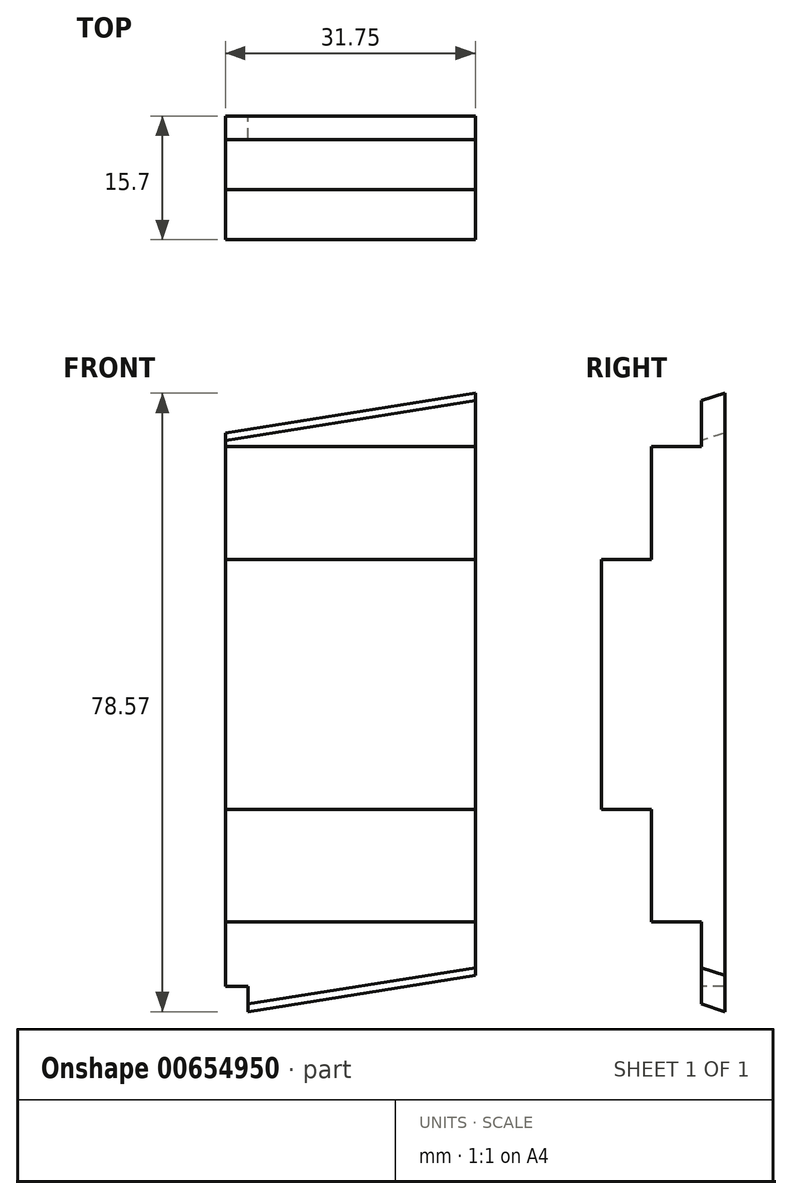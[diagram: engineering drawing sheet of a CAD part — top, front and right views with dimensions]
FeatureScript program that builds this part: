
annotation { "Feature Type Name" : "Feature", "Feature Type Description" : "" }
export const myFeature = defineFeature(function(context is Context, id is Id, definition is map)
    precondition{}
    {
        {
            var Q0;
            Q0=qCreatedBy(makeId("Front.planeOp"),FACE);
            var sketch = newSketch(context, id + "F0", { "sketchPlane" : qUnion([Q0])});
            skLineSegment(sketch, "E0.bottom", {"start": v(0, 0) * mm, "end": v(31.75, 0) * mm});
            skLineSegment(sketch, "E0.top", {"start": v(0, 67.31) * mm, "end": v(31.75, 67.31) * mm});
            skLineSegment(sketch, "E0.left", {"start": v(0, 0) * mm, "end": v(0, 67.31) * mm});
            skLineSegment(sketch, "E0.right", {"start": v(31.75, 0) * mm, "end": v(31.75, 67.31) * mm});
            skLineSegment(sketch, "E1", {"start": v(31.75, 67.31) * mm, "end": v(31.75, 72.4) * mm});
            skLineSegment(sketch, "E2", {"start": v(0, 67.31) * mm, "end": v(31.75, 72.4) * mm});
            skLineSegment(sketch, "E3", {"start": v(31.75, 0) * mm, "end": v(0, -5.08) * mm});
            skLineSegment(sketch, "E4", {"start": v(0, -5.08) * mm, "end": v(0, 0) * mm});
            skSolve(sketch);
        }
        {
            var Q0;
            Q0=makeQuery(id+"F0.imprint","IMPRINT",FACE,{"disambiguationData":[TD([[makeQuery(id+"F0.imprint","IMPRINT",EDGE,{"derivedFrom":sQuery(id+"F0.wireOp",EDGE,"E0.bottom")}),1.0]])]});
            var Q1;
            Q1=makeQuery(id+"F0.imprint","IMPRINT",FACE,{"disambiguationData":[TD([[makeQuery(id+"F0.imprint","IMPRINT",EDGE,{"derivedFrom":sQuery(id+"F0.wireOp",EDGE,"E0.top")}),1.0]])]});
            var Q2;
            Q2=makeQuery(id+"F0.imprint","IMPRINT",FACE,{"disambiguationData":[TD([[makeQuery(id+"F0.imprint","IMPRINT",EDGE,{"derivedFrom":sQuery(id+"F0.wireOp",EDGE,"E0.bottom")}),-1.0]])]});
            extrude(context, id + "F1", {"entities" : qUnion([Q0, Q1, Q2]), "depth" : 3.17 * mm, "offsetDistance" : 25.4 * mm});
        }
        {
            var Q0;
            Q0=makeQuery(id+"F1.opExtrude","CAP_FACE",FACE,{"disambiguationData":[OSD([sQuery(id+"F0.wireOp",EDGE,"E0.left"),sQuery(id+"F0.wireOp",EDGE,"E0.right"),sQuery(id+"F0.wireOp",EDGE,"E1"),sQuery(id+"F0.wireOp",EDGE,"E2"),sQuery(id+"F0.wireOp",EDGE,"E3"),sQuery(id+"F0.wireOp",EDGE,"E4")])],"isStart":false});
            var sketch = newSketch(context, id + "F2", { "sketchPlane" : qUnion([Q0])});
            skLineSegment(sketch, "E5.bottom", {"start": v(0, -5.08) * mm, "end": v(2.54, -5.08) * mm});
            skLineSegment(sketch, "E5.top", {"start": v(0, -2.54) * mm, "end": v(2.54, -2.54) * mm});
            skLineSegment(sketch, "E5.left", {"start": v(0, -5.08) * mm, "end": v(0, -2.54) * mm});
            skLineSegment(sketch, "E5.right", {"start": v(2.54, -5.08) * mm, "end": v(2.54, -2.54) * mm});
            skLineSegment(sketch, "E6", {"start": v(0, -2.36) * mm, "end": v(2.72, -2.36) * mm});
            skLineSegment(sketch, "E7", {"start": v(2.72, -5.08) * mm, "end": v(2.72, -2.36) * mm});
            skSolve(sketch);
        }
        {
            var Q0;
            {var subQ2=sQuery(id+"F2.wireOp",EDGE,"E5.top");Q0=makeQuery(id+"F2.imprint","IMPRINT",FACE,{"disambiguationData":[TD([[makeQuery(id+"F2.imprint","IMPRINT",EDGE,{"derivedFrom":subQ2}),1.0]])]});}
            var Q1;
            {var subQ0=sQuery(id+"F2.wireOp",EDGE,"E5.bottom");Q1=makeQuery(id+"F2.imprint","IMPRINT",FACE,{"disambiguationData":[TD([[makeQuery(id+"F2.imprint","IMPRINT",EDGE,{"derivedFrom":subQ0}),1.0]])]});}
            var Q2;
            {var subQ0=sQuery(id+"F2.wireOp",EDGE,"E5.top");Q2=makeQuery(id+"F2.imprint","IMPRINT",FACE,{"disambiguationData":[TD([[makeQuery(id+"F2.imprint","IMPRINT",EDGE,{"derivedFrom":subQ0}),-1.0]])]});}
            extrude(context, id + "F3", {"entities" : qUnion([Q0, Q1, Q2]), "operationType" : NewBodyOperationType.REMOVE, "oppositeDirection" : true, "depth" : 25.4 * mm, "offsetDistance" : 25.4 * mm});
        }
        {
            var Q0;
            Q0=makeQuery(id+"F3.boolean.opBoolean","COPY",FACE,{"derivedFrom":makeQuery(id+"F3.opExtrude","SWEPT_FACE",FACE,{"disambiguationData":[OSD([sQuery(id+"F2.wireOp",EDGE,"E7")])]})});
            var sketch = newSketch(context, id + "F4", { "sketchPlane" : qUnion([Q0])});
            skLineSegment(sketch, "E8", {"start": v(3.18, -4.65) * mm, "end": v(0, -4.65) * mm});
            skLineSegment(sketch, "E9", {"start": v(3.18, -4.65) * mm, "end": v(0, -5.66) * mm});
            skLineSegment(sketch, "E10", {"start": v(0, -4.65) * mm, "end": v(0, -5.66) * mm});
            skSolve(sketch);
        }
        {
            var Q0;
            Q0=makeQuery(id+"F4.imprint","IMPRINT",FACE,{"disambiguationData":[TD([[makeQuery(id+"F4.imprint","IMPRINT",EDGE,{"derivedFrom":sQuery(id+"F4.wireOp",EDGE,"E8")}),-1.0]])]});
            var Q1;
            Q1=makeQuery(id+"F1.opExtrude","CAP_EDGE",EDGE,{"disambiguationData":[OSD([sQuery(id+"F0.wireOp",EDGE,"E3")])],"isStart":false});
            sweep(context, id + "F5", {"operationType" : NewBodyOperationType.ADD, "profiles" : qUnion([Q0]), "path" : qUnion([Q1])});
        }
        {
            var Q0;
            Q0=makeQuery(id+"F1.opExtrude","SWEPT_FACE",FACE,{"disambiguationData":[OSD([sQuery(id+"F0.wireOp",EDGE,"E0.left"),sQuery(id+"F0.wireOp",EDGE,"E4")])]});
            var sketch = newSketch(context, id + "F6", { "sketchPlane" : qUnion([Q0])});
            skLineSegment(sketch, "E11", {"start": v(0, 67.31) * mm, "end": v(3.18, 67.31) * mm});
            skLineSegment(sketch, "E12", {"start": v(3.18, 67.31) * mm, "end": v(0, 68.33) * mm});
            skLineSegment(sketch, "E13", {"start": v(0, 68.33) * mm, "end": v(0, 67.31) * mm});
            skSolve(sketch);
        }
        {
            var Q0;
            Q0=makeQuery(id+"F6.imprint","IMPRINT",FACE,{"disambiguationData":[TD([[makeQuery(id+"F6.imprint","IMPRINT",EDGE,{"derivedFrom":sQuery(id+"F6.wireOp",EDGE,"E11")}),-1.0]])]});
            var Q1;
            Q1=makeQuery(id+"F1.opExtrude","CAP_EDGE",EDGE,{"disambiguationData":[OSD([sQuery(id+"F0.wireOp",EDGE,"E2")])],"isStart":false});
            sweep(context, id + "F7", {"operationType" : NewBodyOperationType.ADD, "profiles" : qUnion([Q0]), "path" : qUnion([Q1])});
        }
        {
            var Q0;
            {var subQ0=sQuery(id+"F0.wireOp",EDGE,"E1");var subQ1=sQuery(id+"F0.wireOp",EDGE,"E0.right");Q0=makeQuery(id+"F7.boolean.opBoolean","MERGE",FACE,{"derivedFrom":[makeQuery(id+"F5.boolean.opBoolean","MERGE",FACE,{"derivedFrom":[makeQuery(id+"F1.opExtrude","SWEPT_FACE",FACE,{"disambiguationData":[OSD([subQ1,subQ0])]}),makeQuery(id+"F5.opSweep","CAP_FACE",FACE,{"disambiguationData":[OSD([sQuery(id+"F0.wireOp",EDGE,"E0.bottom"),subQ1,sQuery(id+"F0.wireOp",EDGE,"E3"),sQuery(id+"F4.wireOp",EDGE,"E8"),sQuery(id+"F4.wireOp",EDGE,"E9"),sQuery(id+"F4.wireOp",EDGE,"E10")])],"isStart":false})]}),makeQuery(id+"F7.opSweep","CAP_FACE",FACE,{"disambiguationData":[OSD([subQ0,sQuery(id+"F0.wireOp",EDGE,"E2"),sQuery(id+"F6.wireOp",EDGE,"E11"),sQuery(id+"F6.wireOp",EDGE,"E12"),sQuery(id+"F6.wireOp",EDGE,"E13")])],"isStart":false})]});}
            var sketch = newSketch(context, id + "F8", { "sketchPlane" : qUnion([Q0])});
            skLineSegment(sketch, "E14", {"start": v(-3.18, 72.4) * mm, "end": v(0, 73.4) * mm});
            skLineSegment(sketch, "E15", {"start": v(0, 73.4) * mm, "end": v(0, 73.23) * mm});
            skLineSegment(sketch, "E16", {"start": v(0, 73.23) * mm, "end": v(-3.17, 72.21) * mm});
            skLineSegment(sketch, "E17", {"start": v(-3.18, 72.21) * mm, "end": v(-3.18, 72.4) * mm});
            skSolve(sketch);
        }
        {
            var Q0;
            Q0=makeQuery(id+"F8.imprint","IMPRINT",FACE,{"disambiguationData":[TD([[makeQuery(id+"F8.imprint","IMPRINT",EDGE,{"derivedFrom":sQuery(id+"F8.wireOp",EDGE,"E14")}),1.0]])]});
            var Q1;
            {var subQ0=sQuery(id+"F0.wireOp",EDGE,"E2");Q1=makeQuery(id+"F7.boolean.opBoolean","MERGE",EDGE,{"derivedFrom":[makeQuery(id+"F1.opExtrude","CAP_EDGE",EDGE,{"disambiguationData":[OSD([subQ0])],"isStart":false}),makeQuery(id+"F7.opSweep","SWEPT_EDGE",EDGE,{"disambiguationData":[OSD([sQuery(id+"F0.wireOp",EDGE,"E0.left"),subQ0,sQuery(id+"F0.wireOp",EDGE,"E4"),sQuery(id+"F6.wireOp",EDGE,"E11"),sQuery(id+"F6.wireOp",EDGE,"E12")])]})]});}
            sweep(context, id + "F9", {"operationType" : NewBodyOperationType.REMOVE, "profiles" : qUnion([Q0]), "path" : qUnion([Q1])});
        }
        {
            var Q0;
            {var subQ0=sQuery(id+"F0.wireOp",EDGE,"E1");var subQ1=sQuery(id+"F0.wireOp",EDGE,"E0.right");Q0=makeQuery(id+"F7.boolean.opBoolean","MERGE",FACE,{"derivedFrom":[makeQuery(id+"F5.boolean.opBoolean","MERGE",FACE,{"derivedFrom":[makeQuery(id+"F1.opExtrude","SWEPT_FACE",FACE,{"disambiguationData":[OSD([subQ1,subQ0])]}),makeQuery(id+"F5.opSweep","CAP_FACE",FACE,{"disambiguationData":[OSD([sQuery(id+"F0.wireOp",EDGE,"E0.bottom"),subQ1,sQuery(id+"F0.wireOp",EDGE,"E3"),sQuery(id+"F4.wireOp",EDGE,"E8"),sQuery(id+"F4.wireOp",EDGE,"E9"),sQuery(id+"F4.wireOp",EDGE,"E10")])],"isStart":false})]}),makeQuery(id+"F7.opSweep","CAP_FACE",FACE,{"disambiguationData":[OSD([subQ0,sQuery(id+"F0.wireOp",EDGE,"E2"),sQuery(id+"F6.wireOp",EDGE,"E11"),sQuery(id+"F6.wireOp",EDGE,"E12"),sQuery(id+"F6.wireOp",EDGE,"E13")])],"isStart":false})]});}
            var sketch = newSketch(context, id + "F10", { "sketchPlane" : qUnion([Q0])});
            skLineSegment(sketch, "E18", {"start": v(-3.18, 0) * mm, "end": v(0, -1.02) * mm});
            skLineSegment(sketch, "E19", {"start": v(0, -1.02) * mm, "end": v(0, -0.84) * mm});
            skLineSegment(sketch, "E20", {"start": v(0, -0.84) * mm, "end": v(-3.18, 0.18) * mm});
            skLineSegment(sketch, "E21", {"start": v(-3.18, 0.18) * mm, "end": v(-3.18, 0) * mm});
            skSolve(sketch);
        }
        {
            var Q0;
            Q0=makeQuery(id+"F10.imprint","IMPRINT",FACE,{"disambiguationData":[TD([[makeQuery(id+"F10.imprint","IMPRINT",EDGE,{"derivedFrom":sQuery(id+"F10.wireOp",EDGE,"E18")}),1.0]])]});
            var Q1;
            {var subQ0=sQuery(id+"F0.wireOp",EDGE,"E3");Q1=makeQuery(id+"F5.boolean.opBoolean","MERGE",EDGE,{"derivedFrom":[makeQuery(id+"F1.opExtrude","CAP_EDGE",EDGE,{"disambiguationData":[OSD([subQ0])],"isStart":false}),makeQuery(id+"F5.opSweep","SWEPT_EDGE",EDGE,{"disambiguationData":[OSD([subQ0,sQuery(id+"F2.wireOp",EDGE,"E7"),sQuery(id+"F4.wireOp",EDGE,"E8"),sQuery(id+"F4.wireOp",EDGE,"E9")])]})]});}
            sweep(context, id + "F11", {"operationType" : NewBodyOperationType.REMOVE, "profiles" : qUnion([Q0]), "path" : qUnion([Q1])});
        }
        {
            var Q0;
            {var subQ0=sQuery(id+"F0.wireOp",EDGE,"E0.left");Q0=makeQuery(id+"F7.boolean.opBoolean","MERGE",FACE,{"derivedFrom":[makeQuery(id+"F1.opExtrude","SWEPT_FACE",FACE,{"disambiguationData":[OSD([subQ0,sQuery(id+"F0.wireOp",EDGE,"E4")])]}),makeQuery(id+"F7.opSweep","CAP_FACE",FACE,{"disambiguationData":[OSD([sQuery(id+"F0.wireOp",EDGE,"E0.top"),subQ0,sQuery(id+"F0.wireOp",EDGE,"E2"),sQuery(id+"F6.wireOp",EDGE,"E11"),sQuery(id+"F6.wireOp",EDGE,"E12"),sQuery(id+"F6.wireOp",EDGE,"E13")])],"isStart":true})]});}
            var sketch = newSketch(context, id + "F12", { "sketchPlane" : qUnion([Q0])});
            skLineSegment(sketch, "E22", {"start": v(3.18, -2.36) * mm, "end": v(0, -2.36) * mm});
            skLineSegment(sketch, "E23", {"start": v(0, -2.36) * mm, "end": v(0, -2.18) * mm});
            skLineSegment(sketch, "E24", {"start": v(0, -2.18) * mm, "end": v(3.18, -2.18) * mm});
            skLineSegment(sketch, "E25", {"start": v(3.18, -2.18) * mm, "end": v(3.18, -2.36) * mm});
            skSolve(sketch);
        }
        {
            var Q0;
            Q0=makeQuery(id+"F12.imprint","IMPRINT",FACE,{"disambiguationData":[TD([[makeQuery(id+"F12.imprint","IMPRINT",EDGE,{"derivedFrom":sQuery(id+"F12.wireOp",EDGE,"E22")}),1.0]])]});
            var Q1;
            {var subQ0=sQuery(id+"F2.wireOp",EDGE,"E7");var subQ1=sQuery(id+"F0.wireOp",EDGE,"E3");Q1=makeQuery(id+"F5.boolean.opBoolean","MERGE",EDGE,{"derivedFrom":[makeQuery(id+"F3.boolean.opBoolean","INTERSECT",EDGE,{"derivedFrom":[makeQuery(id+"F1.opExtrude","CAP_FACE",FACE,{"disambiguationData":[OSD([sQuery(id+"F0.wireOp",EDGE,"E0.left"),sQuery(id+"F0.wireOp",EDGE,"E0.right"),sQuery(id+"F0.wireOp",EDGE,"E1"),sQuery(id+"F0.wireOp",EDGE,"E2"),subQ1,sQuery(id+"F0.wireOp",EDGE,"E4")])],"isStart":true}),makeQuery(id+"F3.opExtrude","SWEPT_FACE",FACE,{"disambiguationData":[OSD([subQ0])]})]}),makeQuery(id+"F5.opSweep","CAP_EDGE",EDGE,{"disambiguationData":[OSD([subQ1,subQ0,sQuery(id+"F4.wireOp",EDGE,"E10")])],"isStart":true})]});}
            var Q2;
            Q2=makeQuery(id+"F3.boolean.opBoolean","INTERSECT",EDGE,{"derivedFrom":[makeQuery(id+"F1.opExtrude","CAP_FACE",FACE,{"disambiguationData":[OSD([sQuery(id+"F0.wireOp",EDGE,"E0.left"),sQuery(id+"F0.wireOp",EDGE,"E0.right"),sQuery(id+"F0.wireOp",EDGE,"E1"),sQuery(id+"F0.wireOp",EDGE,"E2"),sQuery(id+"F0.wireOp",EDGE,"E3"),sQuery(id+"F0.wireOp",EDGE,"E4")])],"isStart":true}),makeQuery(id+"F3.opExtrude","SWEPT_FACE",FACE,{"disambiguationData":[OSD([sQuery(id+"F2.wireOp",EDGE,"E6")])]})]});
            sweep(context, id + "F13", {"operationType" : NewBodyOperationType.REMOVE, "profiles" : qUnion([Q0]), "path" : qUnion([Q1, Q2])});
        }
        {
            var Q0;
            {var subQ0=sQuery(id+"F0.wireOp",EDGE,"E2");var subQ1=sQuery(id+"F0.wireOp",EDGE,"E3");Q0=makeQuery(id+"F7.boolean.opBoolean","MERGE",FACE,{"derivedFrom":[makeQuery(id+"F5.boolean.opBoolean","MERGE",FACE,{"derivedFrom":[makeQuery(id+"F1.opExtrude","CAP_FACE",FACE,{"disambiguationData":[OSD([sQuery(id+"F0.wireOp",EDGE,"E0.left"),sQuery(id+"F0.wireOp",EDGE,"E0.right"),sQuery(id+"F0.wireOp",EDGE,"E1"),subQ0,subQ1,sQuery(id+"F0.wireOp",EDGE,"E4")])],"isStart":true}),makeQuery(id+"F5.opSweep","SWEPT_FACE",FACE,{"disambiguationData":[OSD([subQ1,sQuery(id+"F4.wireOp",EDGE,"E10")])]})]}),makeQuery(id+"F7.opSweep","SWEPT_FACE",FACE,{"disambiguationData":[OSD([subQ0,sQuery(id+"F6.wireOp",EDGE,"E13")])]})]});}
            extrude(context, id + "F14", {"entities" : qUnion([Q0]), "operationType" : NewBodyOperationType.REMOVE, "oppositeDirection" : true, "depth" : 0.18 * mm, "offsetDistance" : 25.4 * mm});
        }
        {
            var Q0;
            Q0=makeQuery(id+"F1.opExtrude","CAP_FACE",FACE,{"disambiguationData":[OSD([sQuery(id+"F0.wireOp",EDGE,"E0.left"),sQuery(id+"F0.wireOp",EDGE,"E0.right"),sQuery(id+"F0.wireOp",EDGE,"E1"),sQuery(id+"F0.wireOp",EDGE,"E2"),sQuery(id+"F0.wireOp",EDGE,"E3"),sQuery(id+"F0.wireOp",EDGE,"E4")])],"isStart":false});
            var sketch = newSketch(context, id + "F15", { "sketchPlane" : qUnion([Q0])});
            skLineSegment(sketch, "E26", {"start": v(31.75, 36.2) * mm, "end": v(0, 36.2) * mm});
            skLineSegment(sketch, "E27", {"start": v(31.75, 52.07) * mm, "end": v(31.75, 20.32) * mm});
            skLineSegment(sketch, "E28", {"start": v(31.75, 52.07) * mm, "end": v(0, 52.07) * mm});
            skLineSegment(sketch, "E29", {"start": v(31.75, 20.32) * mm, "end": v(0, 20.32) * mm});
            skLineSegment(sketch, "E30", {"start": v(0, 52.07) * mm, "end": v(0, 20.32) * mm});
            skLineSegment(sketch, "E31", {"start": v(31.75, 20.32) * mm, "end": v(31.75, 6.02) * mm});
            skLineSegment(sketch, "E32", {"start": v(31.75, 52.07) * mm, "end": v(31.75, 66.37) * mm});
            skLineSegment(sketch, "E33", {"start": v(31.75, 66.37) * mm, "end": v(0, 66.37) * mm});
            skLineSegment(sketch, "E34", {"start": v(0, 66.37) * mm, "end": v(0, 52.07) * mm});
            skLineSegment(sketch, "E35", {"start": v(31.75, 6.02) * mm, "end": v(0, 6.02) * mm});
            skLineSegment(sketch, "E36", {"start": v(0, 6.02) * mm, "end": v(0, 20.32) * mm});
            skSolve(sketch);
        }
        {
            var Q0;
            {var subQ0=sQuery(id+"F15.wireOp",EDGE,"E26");Q0=makeQuery(id+"F15.imprint","IMPRINT",FACE,{"disambiguationData":[TD([[makeQuery(id+"F15.imprint","IMPRINT",EDGE,{"derivedFrom":subQ0}),-1.0]])]});}
            var Q1;
            {var subQ0=sQuery(id+"F15.wireOp",EDGE,"E26");Q1=makeQuery(id+"F15.imprint","IMPRINT",FACE,{"disambiguationData":[TD([[makeQuery(id+"F15.imprint","IMPRINT",EDGE,{"derivedFrom":subQ0}),1.0]])]});}
            extrude(context, id + "F16", {"entities" : qUnion([Q0, Q1]), "operationType" : NewBodyOperationType.ADD, "depth" : 12.7 * mm, "offsetDistance" : 25.4 * mm});
        }
        {
            var Q0;
            Q0=makeQuery(id+"F15.imprint","IMPRINT",FACE,{"disambiguationData":[TD([[makeQuery(id+"F15.imprint","IMPRINT",EDGE,{"derivedFrom":sQuery(id+"F15.wireOp",EDGE,"E28")}),-1.0]])]});
            var Q1;
            Q1=makeQuery(id+"F15.imprint","IMPRINT",FACE,{"disambiguationData":[TD([[makeQuery(id+"F15.imprint","IMPRINT",EDGE,{"derivedFrom":sQuery(id+"F15.wireOp",EDGE,"E29")}),1.0]])]});
            extrude(context, id + "F17", {"entities" : qUnion([Q0, Q1]), "operationType" : NewBodyOperationType.ADD, "depth" : 6.35 * mm, "offsetDistance" : 25.4 * mm});
        }
    });
